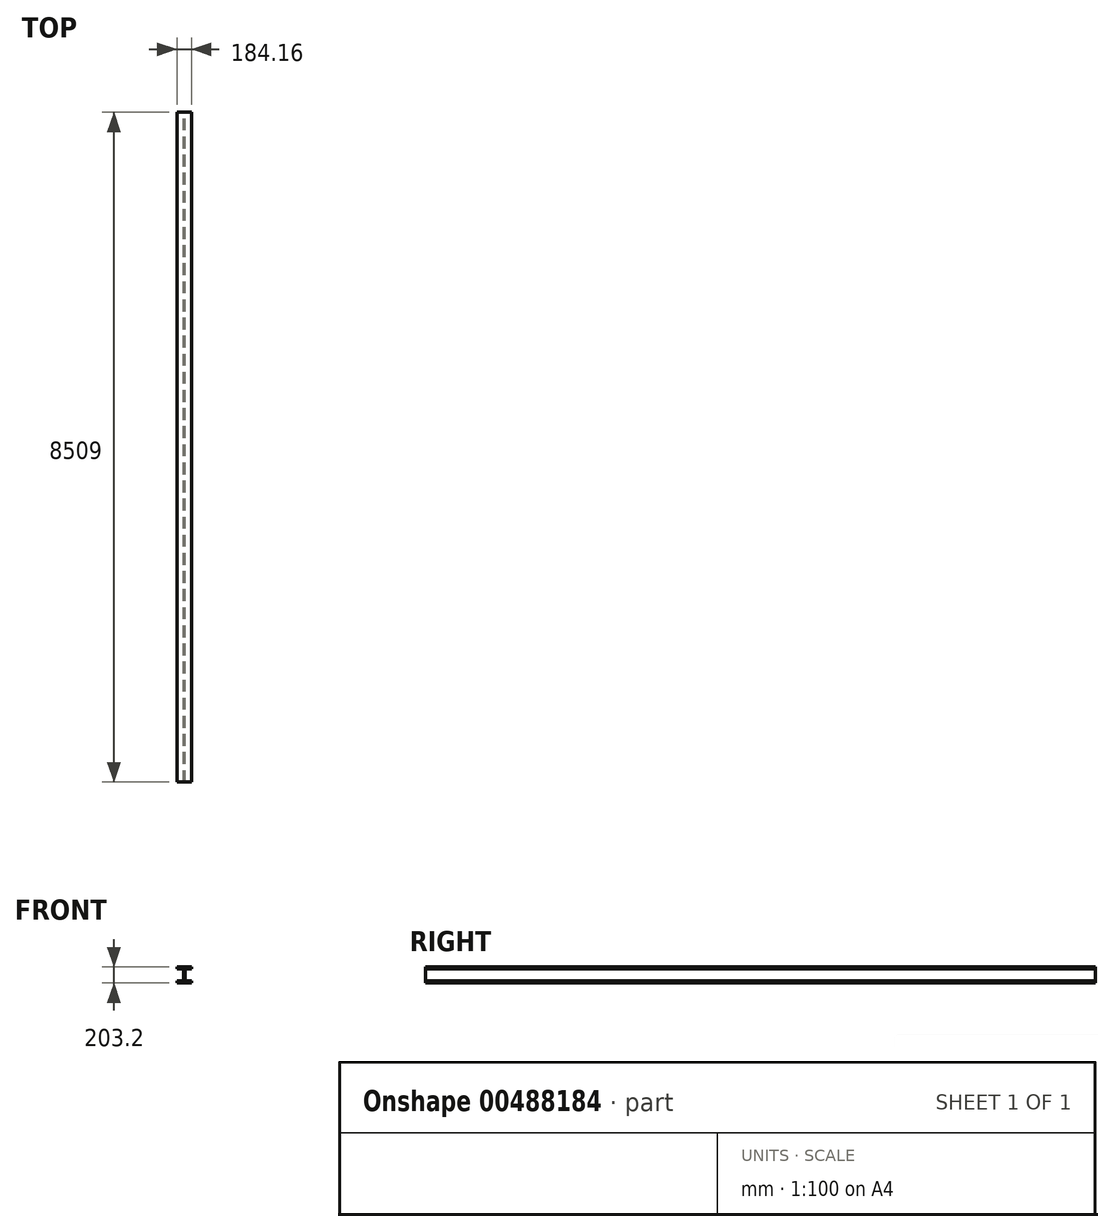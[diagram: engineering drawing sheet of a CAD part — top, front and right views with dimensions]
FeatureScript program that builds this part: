
annotation { "Feature Type Name" : "Feature", "Feature Type Description" : "" }
export const myFeature = defineFeature(function(context is Context, id is Id, definition is map)
    precondition{}
    {
        {
            var Q0;
            Q0=qCreatedBy(makeId("Front.planeOp"),FACE);
            var sketch = newSketch(context, id + "F0", { "sketchPlane" : qUnion([Q0])});
            skLineSegment(sketch, "E0", {"start": v(92.08, -76.2) * mm, "end": v(12.07, -76.2) * mm});
            skLineSegment(sketch, "E1", {"start": v(9.52, -73.66) * mm, "end": v(9.52, 73.66) * mm});
            skLineSegment(sketch, "E2", {"start": v(12.07, 76.2) * mm, "end": v(92.08, 76.2) * mm});
            skLineSegment(sketch, "E3", {"start": v(-92.08, 76.2) * mm, "end": v(-12.07, 76.2) * mm});
            skLineSegment(sketch, "E4", {"start": v(-9.53, 73.66) * mm, "end": v(-9.53, -73.66) * mm});
            skLineSegment(sketch, "E5", {"start": v(-12.06, -76.2) * mm, "end": v(-92.08, -76.2) * mm});
            skLineSegment(sketch, "E6", {"start": v(0, 0) * mm, "end": v(-9.52, 0) * mm, "construction": true});
            skLineSegment(sketch, "E7", {"start": v(0, 0) * mm, "end": v(9.52, 0) * mm, "construction": true});
            skLineSegment(sketch, "E8", {"start": v(0, 0) * mm, "end": v(0, 101.6) * mm, "construction": true});
            skLineSegment(sketch, "E9", {"start": v(0, 0) * mm, "end": v(0, -101.6) * mm, "construction": true});
            skPoint(sketch, "E10.visualSharp", {"position": v(-9.53, 76.2) * mm});
            skArc(sketch, "E10.filletArc", {"start": v(-9.52, 73.66) * mm, "mid": v(-10.27, 75.46) * mm, "end": v(-12.07, 76.2) * mm});
            skPoint(sketch, "E11.visualSharp", {"position": v(9.53, 76.2) * mm});
            skArc(sketch, "E11.filletArc", {"start": v(12.07, 76.2) * mm, "mid": v(10.27, 75.46) * mm, "end": v(9.52, 73.66) * mm});
            skPoint(sketch, "E12.visualSharp", {"position": v(9.53, -76.2) * mm});
            skArc(sketch, "E12.filletArc", {"start": v(9.52, -73.66) * mm, "mid": v(10.27, -75.46) * mm, "end": v(12.07, -76.2) * mm});
            skPoint(sketch, "E13.visualSharp", {"position": v(-9.53, -76.2) * mm});
            skArc(sketch, "E13.filletArc", {"start": v(-12.06, -76.2) * mm, "mid": v(-10.27, -75.46) * mm, "end": v(-9.52, -73.66) * mm});
            skPoint(sketch, "E14.visualSharp", {"position": v(-92.08, 101.6) * mm});
            skPoint(sketch, "E15.visualSharp", {"position": v(92.08, 101.6) * mm});
            skPoint(sketch, "E16.visualSharp", {"position": v(92.08, 76.2) * mm});
            skPoint(sketch, "E17.visualSharp", {"position": v(92.08, -101.6) * mm});
            skPoint(sketch, "E18.visualSharp", {"position": v(-92.08, -76.2) * mm});
            skPoint(sketch, "E19.visualSharp", {"position": v(-92.08, -101.6) * mm});
            skLineSegment(sketch, "E20", {"start": v(92.08, -76.2) * mm, "end": v(92.08, -101.6) * mm});
            skLineSegment(sketch, "E21", {"start": v(-92.08, -76.2) * mm, "end": v(-92.08, -101.6) * mm});
            skLineSegment(sketch, "E22", {"start": v(-92.08, 101.6) * mm, "end": v(-92.08, 76.2) * mm});
            skLineSegment(sketch, "E23", {"start": v(92.08, 101.6) * mm, "end": v(92.08, 76.2) * mm});
            skLineSegment(sketch, "E24", {"start": v(-92.08, 101.6) * mm, "end": v(92.08, 101.6) * mm});
            skLineSegment(sketch, "E25", {"start": v(-92.07, -101.6) * mm, "end": v(92.08, -101.6) * mm});
            skSolve(sketch);
        }
        {
            var Q0;
            Q0=makeQuery(id+"F0.imprint","IMPRINT",FACE,{"disambiguationData":[TD([[makeQuery(id+"F0.imprint","IMPRINT",EDGE,{"derivedFrom":sQuery(id+"F0.wireOp",EDGE,"E0")}),1.0]])]});
            extrude(context, id + "F1", {"entities" : qUnion([Q0]), "depth" : 8509 * mm});
        }
    });
